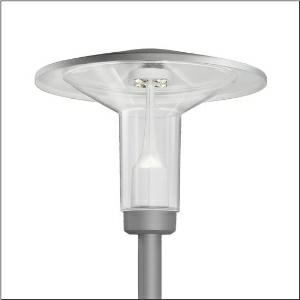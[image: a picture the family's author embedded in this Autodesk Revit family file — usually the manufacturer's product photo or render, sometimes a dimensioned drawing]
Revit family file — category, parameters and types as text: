
# Revit family: laterne_iq___st1_2a_5xa5255af14hp_61c0
name_source: partatom
category: Lighting Fixtures
units: mm (PartAtom-declared; Revit-internal decimal feet)

## family parameters
Cut with Voids When Loaded = No
Host = Face
Light Source = No
Part Type = Normal
Room Calculation Point = No
Round Connector Dimension = Use Diameter
Shared = No

## types (1)
- --- (1 x LED, 3910 lm, 33.6 W, 2200K)
    Apparent Load = 34 VA
    CIE Flux Codes = 25 63 94 98 100
    Color Rendering = 70
    Color Temperature = 2200K
    Default Elevation = 1800 mm
    Description = Lantern iQ, mast luminaire, Module 540 iQ-SR, primary light control with 3 zone facetted reflector, of plastic, silver coated, highly specular, structured, primary optical cover: cover, of PMMA, transparent, light distribution: ST1.2a, light emission: direct distribution, primary light characteristic: asymmetric, installation type: post-top, LED, High Power LED, rated luminous flux: 3.910lm, luminous efficacy: 116lm/W, light colour: 722, colour temperature: 2200K, control gear: iQ Street-Remote, control: pre-setting: logarithmic dimming characteristic, Street-Remote, Auto-Match, Temp-Guard, Lumen-Switch, Night-Set, Smart-Wire, Light-Fading, Desk-Remote (wireless, voltage-free reading and setting of iQ features in the workshop via application-optimized NFC function/RFID function), optimised constant luminous flux control (CLO 2.0), with terminal, 6-pole, max. 2.5mm², mains connection: 230..240V, AC, 50/60Hz, start of lifetime: 34W, end of service life: 36W, reduction: 15W, luminaire housing, upper part, of glass-fibre reinforced polyester, coated, Siteco® metallic grey (DB 702S), diameter: 750mm, height: 583mm, spigot size: d x l = 76 x 70mm (post-top) | with reducer (optional accessory) 60 x 70mm, mounting height: 3..5m, post-top mast mounting element, of diecast aluminium, coated, Siteco® metallic grey (DB 702S), Module 540 iQ-SR, traffic white (RAL 9016), equipment: Power, protection rating (complete): IP65, insulation class (complete): insulation class II (safety insulation), certification: CE, ENEC, VDE, packaging unit: 1 piece

Light Distribution: ST1.2a
    Height = 583 mm
    Lamp = 1 x LED
    Lamp Light Flux = 3910 lm
    Lamp Power = 33.6 W
    Lamp count = 1
    Length = 750 mm
    Luminous efficacy = 116 lm/W
    Manufacturer = Siteco
    ModVariant = No
    Model = 5XA5255AF14HP
    Number of Poles = 1
    OnlyDefault = Yes
    Power Factor = 1
    Product Name = Laterne iQ | ST1.2a
    Product group = mast luminaire | pylon top
    ProductGroupID = 6100
    Protection Class = Protection class II
    Protection Degree = IP 65
    RLX_Detail_Level = 1
    RLX_Emergency_Light_Flux = 0 lm
    RLX_Emergency_Type = 0
    RLX_Emergency_Type_DB = No
    RlxData = <blob elided: 34201 chars, md5=d53e1fcf>
    Socket = socket
    Standby Power = 0 W
    System Light Flux = 3910 lm
    System Power = 34 W
    Type Comments = factory setting: luminous flux: 100 % | dim-lin: 254 | 695 mA
    Type Image = l_1006050.jpg
    URL = http://relux.com
    VarID = @adj_214845
    Voltage = 0 V
    Weight = 0.00 kg
    Width = 0 mm  [stored 0 ft]

note: [stored X ft] marks values corroborated as IEEE doubles in the binary element streams (Revit-internal decimal feet)

## geometry (parser evidence)
native form markers: Blend x4, Sweep x10
no freeform markers — native parametric forms only
